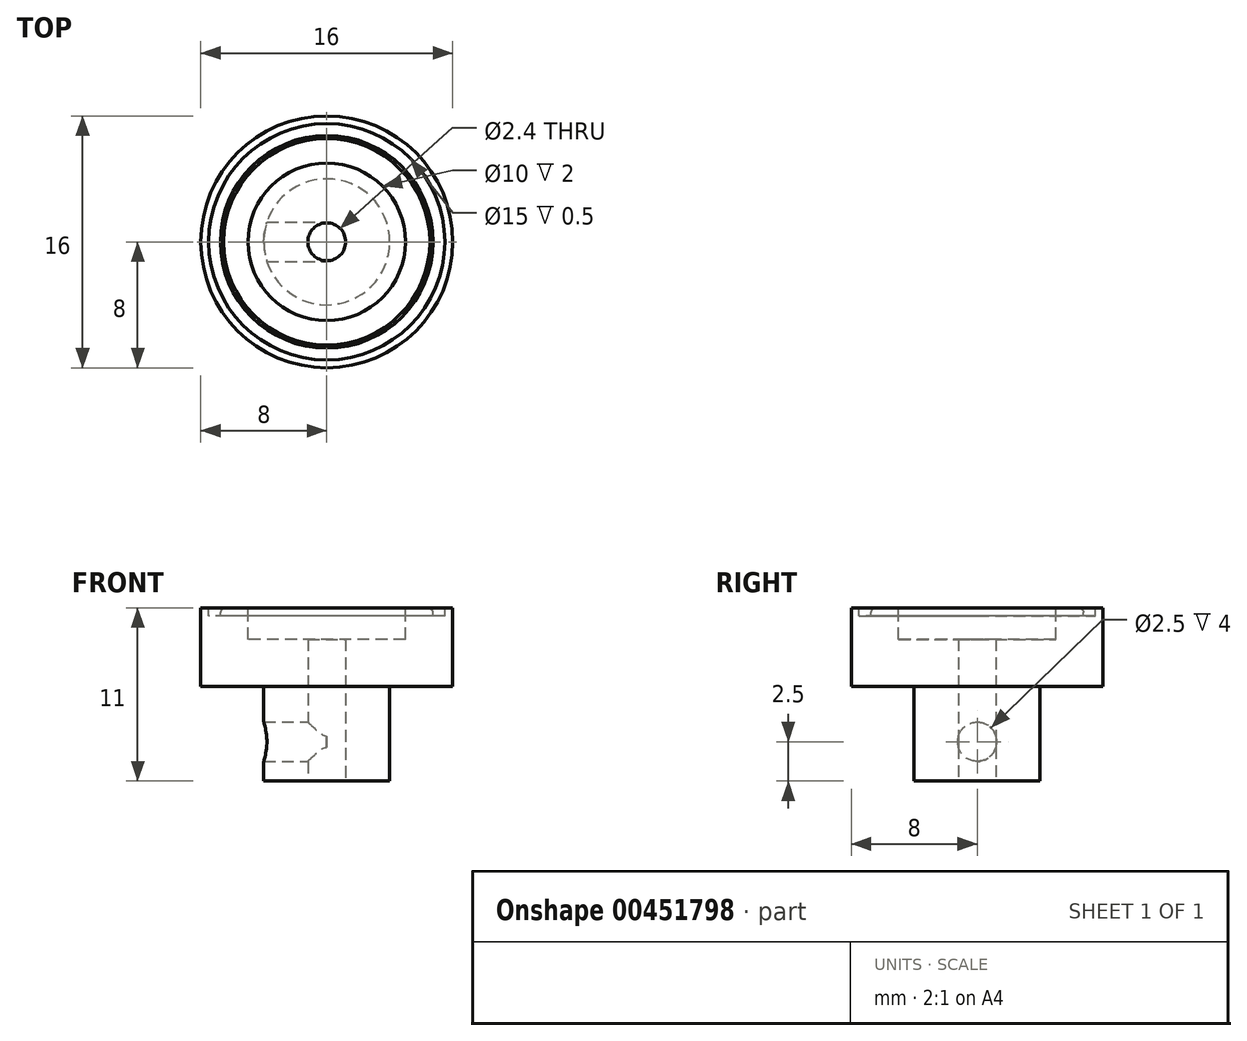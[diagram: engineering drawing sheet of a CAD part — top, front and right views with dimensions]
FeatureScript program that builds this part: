
annotation { "Feature Type Name" : "Feature", "Feature Type Description" : "" }
export const myFeature = defineFeature(function(context is Context, id is Id, definition is map)
    precondition{}
    {
        {
            var Q0;
            Q0=qCreatedBy(makeId("Top.planeOp"),FACE);
            var sketch = newSketch(context, id + "F0", { "sketchPlane" : qUnion([Q0])});
            skCircle(sketch, "E0", {"center": v(0, 0) * mm, "radius": 8 * mm});
            skSolve(sketch);
        }
        {
            var Q0;
            Q0=qSketchRegion(id+"F0",true);
            extrude(context, id + "F1", {"entities" : qUnion([Q0]), "depth" : 5 * mm});
        }
        {
            var Q0;
            Q0=makeQuery(id+"F1.opExtrude","CAP_FACE",FACE,{"disambiguationData":[OSD([sQuery(id+"F0.wireOp",EDGE,"E0")])],"isStart":true});
            var sketch = newSketch(context, id + "F2", { "sketchPlane" : qUnion([Q0])});
            skCircle(sketch, "E1", {"center": v(0, 0) * mm, "radius": 4 * mm});
            skSolve(sketch);
        }
        {
            var Q0;
            Q0=qSketchRegion(id+"F2",true);
            extrude(context, id + "F3", {"entities" : qUnion([Q0]), "operationType" : NewBodyOperationType.ADD, "depth" : 6 * mm});
        }
        {
            var Q0;
            Q0=makeQuery(id+"F3.opExtrude","CAP_FACE",FACE,{"disambiguationData":[OSD([sQuery(id+"F2.wireOp",EDGE,"E1")])],"isStart":false});
            var sketch = newSketch(context, id + "F4", { "sketchPlane" : qUnion([Q0])});
            skCircle(sketch, "E2", {"center": v(0, 0) * mm, "radius": 1.2 * mm});
            skSolve(sketch);
        }
        {
            var Q0;
            Q0=qSketchRegion(id+"F4",true);
            extrude(context, id + "F5", {"entities" : qUnion([Q0]), "operationType" : NewBodyOperationType.REMOVE, "oppositeDirection" : true, "depth" : 9 * mm});
        }
        {
            var Q0;
            Q0=makeQuery(id+"F1.opExtrude","CAP_FACE",FACE,{"disambiguationData":[OSD([sQuery(id+"F0.wireOp",EDGE,"E0")])],"isStart":false});
            var sketch = newSketch(context, id + "F6", { "sketchPlane" : qUnion([Q0])});
            skCircle(sketch, "E3", {"center": v(0, 0) * mm, "radius": 5 * mm});
            skSolve(sketch);
        }
        {
            var Q0;
            Q0=qSketchRegion(id+"F6",true);
            extrude(context, id + "F7", {"entities" : qUnion([Q0]), "operationType" : NewBodyOperationType.REMOVE, "oppositeDirection" : true, "depth" : 2 * mm});
        }
        {
            var Q0;
            Q0=makeQuery(id+"F1.opExtrude","CAP_FACE",FACE,{"disambiguationData":[OSD([sQuery(id+"F0.wireOp",EDGE,"E0")])],"isStart":false});
            var sketch = newSketch(context, id + "F8", { "sketchPlane" : qUnion([Q0])});
            skCircle(sketch, "E4", {"center": v(0, 0) * mm, "radius": 7.5 * mm});
            skCircle(sketch, "E5", {"center": v(0, 0) * mm, "radius": 6.75 * mm});
            skSolve(sketch);
        }
        {
            var Q0;
            Q0=makeQuery(id+"F8.imprint","IMPRINT",FACE,{"disambiguationData":[TD([[makeQuery(id+"F8.imprint","IMPRINT",EDGE,{"derivedFrom":sQuery(id+"F8.wireOp",EDGE,"E4")}),1.0]])]});
            extrude(context, id + "F9", {"entities" : qUnion([Q0]), "operationType" : NewBodyOperationType.REMOVE, "oppositeDirection" : true, "depth" : 0.5 * mm});
        }
        {
            var Q0;
            Q0=makeQuery(id+"F9.boolean.opBoolean","COPY",EDGE,{"derivedFrom":makeQuery(id+"F9.opExtrude","CAP_EDGE",EDGE,{"disambiguationData":[OSD([sQuery(id+"F8.wireOp",EDGE,"E5")])],"isStart":true})});
            chamfer(context, id + "F10", {"entities" : qUnion([Q0]), "width" : 0.2 * mm, "tangentPropagation" : true});
        }
        {
            var Q0;
            {var subQ0=sQuery(id+"F8.wireOp",EDGE,"E5");Q0=makeQuery(id+"F10.opChamfer","BLEND_EDGE",EDGE,{"blendedFrom":[makeQuery(id+"F9.boolean.opBoolean","COPY",EDGE,{"derivedFrom":makeQuery(id+"F9.opExtrude","CAP_EDGE",EDGE,{"disambiguationData":[OSD([subQ0])],"isStart":true})}),makeQuery(id+"F9.boolean.opBoolean","COPY",FACE,{"derivedFrom":makeQuery(id+"F9.opExtrude","SWEPT_FACE",FACE,{"disambiguationData":[OSD([subQ0])]})})],"blendedInto":[makeQuery(id+"F9.boolean.opBoolean","COPY",FACE,{"derivedFrom":makeQuery(id+"F9.opExtrude","SWEPT_FACE",FACE,{"disambiguationData":[OSD([subQ0])]})})]});}
            var Q1;
            Q1=makeQuery(id+"F5.boolean.opBoolean","COPY",EDGE,{"derivedFrom":makeQuery(id+"F5.opExtrude","CAP_EDGE",EDGE,{"disambiguationData":[OSD([sQuery(id+"F4.wireOp",EDGE,"E2")])],"isStart":false})});
            var Q2;
            Q2=makeQuery(id+"F5.boolean.opBoolean","COPY",EDGE,{"derivedFrom":makeQuery(id+"F5.opExtrude","CAP_EDGE",EDGE,{"disambiguationData":[OSD([sQuery(id+"F4.wireOp",EDGE,"E2")])],"isStart":true})});
            fillet(context, id + "F11", {"entities" : qUnion([Q0, Q1, Q2]), "radius" : 0.2 * mm, "tangentPropagation" : true, "allowEdgeOverflow" : false});
        }
        {
            var Q0;
            Q0=qCreatedBy(makeId("Top.planeOp"),FACE);
            cPlane(context, id + "F12", {"entities" : qUnion([Q0]), "cplaneType" : CPlaneType.OFFSET, "offset" : 5 * mm, "width" : 150 * mm, "height" : 150 * mm});
        }
        {
            var Q0;
            Q0=qCreatedBy(makeId("Right.planeOp"),FACE);
            var sketch = newSketch(context, id + "F13", { "sketchPlane" : qUnion([Q0])});
            skPoint(sketch, "E6", {"position": v(0, -3.5) * mm});
            skCircle(sketch, "E7", {"center": v(0, -3.5) * mm, "radius": 1.25 * mm});
            skSolve(sketch);
        }
        {
            var Q0;
            Q0=qSketchRegion(id+"F13",true);
            extrude(context, id + "F14", {"entities" : qUnion([Q0]), "operationType" : NewBodyOperationType.REMOVE, "oppositeDirection" : true, "depth" : 4.5 * mm});
        }
    });
